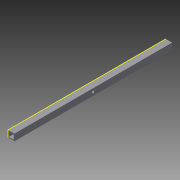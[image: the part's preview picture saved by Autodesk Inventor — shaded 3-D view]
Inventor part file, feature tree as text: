
AUTODESK INVENTOR PART (.ipt)
format: ipt  version: 2013 (Build 170138000, 138)  size: 109,568 bytes
history: native  units: in
note: dims shown in document units (in); Inventor stores cm internally (conversion verified against a paired STEP export)
features: sketch x3, extrude x2, hole x1
ambient origin geometry x8: Origin, YZ Plane, XZ Plane, XY Plane, X Axis, Y Axis, Z Axis, Center Point
bodies: Solid1 (feature_tree)
feature tree (6):
  extrude  "Extrusion1"  Depth=0.5in
  hole  "Hole1"  [1 undecoded]
  extrude  "Extrusion2"  Depth=0.168in
  sketch  "Sketch1"  dims[d0=0.5in d1=0.5in]
  sketch  "Sketch3"  dims[d3=12.0in d4=0.0in d5=0.07in]
  sketch  "Sketch4"  dims[d6=0.1875in d7=0.75in d8=0.375in d9=0.25in d10=0.5635in d11=1.0in d12=0.8108in d13=0.168in d14=0.25in d15=0.168in d16=0.25in d17=0.5in d18=0.0in]
note: 1 required parameter value undecoded (feature->parameter linkage not recoverable at this tier; creation-order binding heuristic only, values carry confidence <= 0.55)
